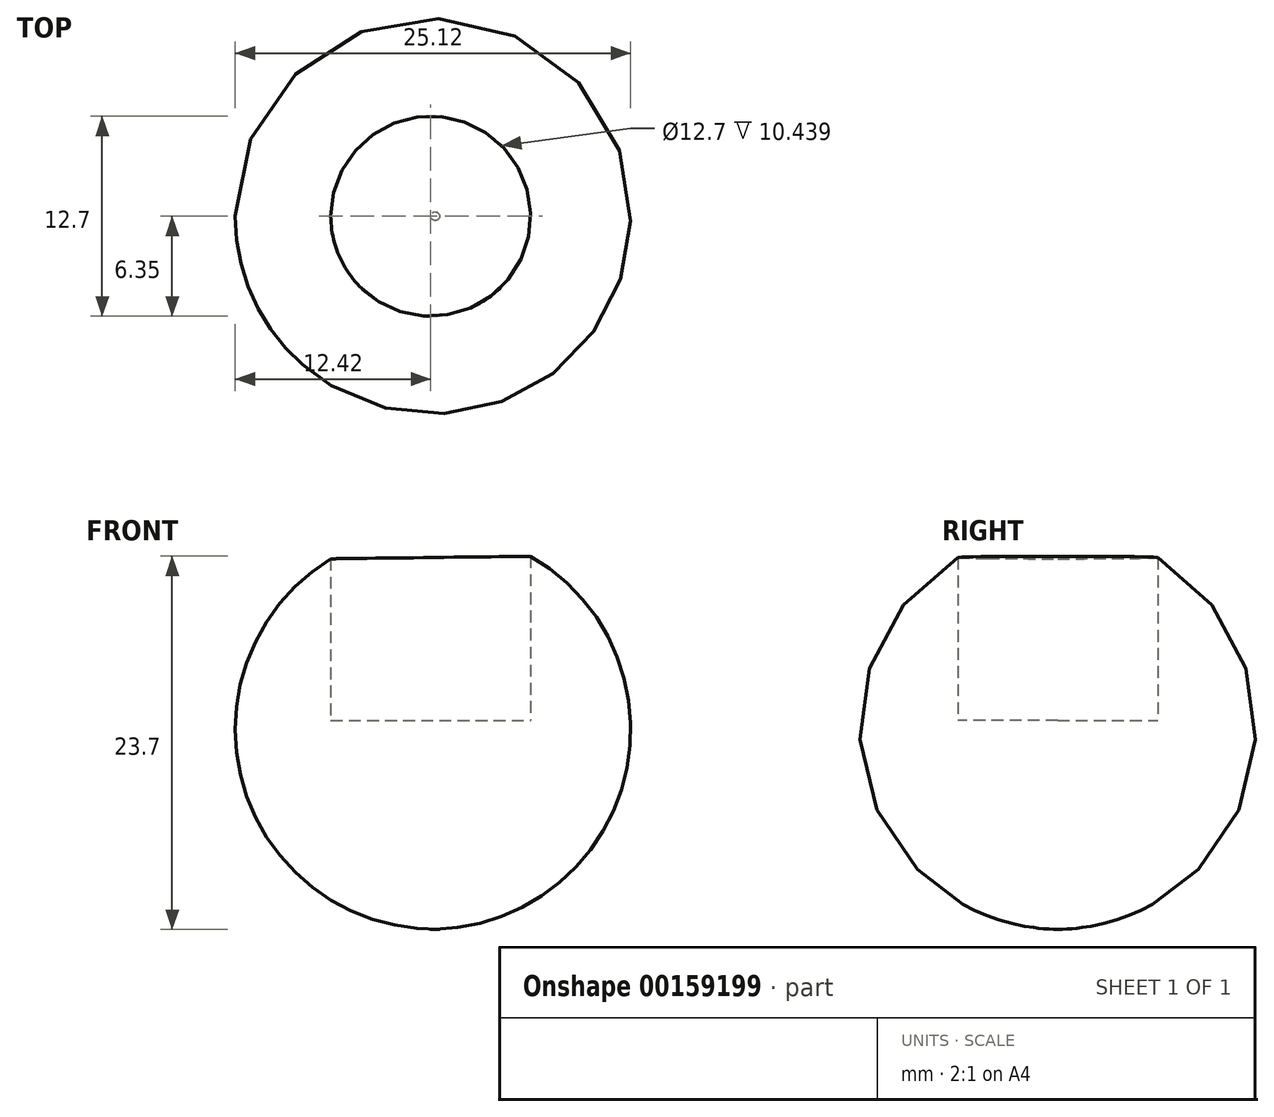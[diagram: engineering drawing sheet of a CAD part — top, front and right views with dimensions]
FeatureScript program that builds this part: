
annotation { "Feature Type Name" : "Feature", "Feature Type Description" : "" }
export const myFeature = defineFeature(function(context is Context, id is Id, definition is map)
    precondition{}
    {
        {
            var Q0;
            Q0=qCreatedBy(makeId("Front.planeOp"),FACE);
            var sketch = newSketch(context, id + "F0", { "sketchPlane" : qUnion([Q0])});
            skArc(sketch, "E0", {"start": v(0, 12.14) * mm, "mid": v(-12.42, -0.7) * mm, "end": v(0.28, -13.26) * mm});
            skLineSegment(sketch, "E1", {"start": v(0, 12.14) * mm, "end": v(0.28, -13.26) * mm});
            skSolve(sketch);
        }
        {
            var Q0;
            Q0=makeQuery(id+"F0.imprint","IMPRINT",FACE,{"disambiguationData":[TD([[makeQuery(id+"F0.imprint","IMPRINT",EDGE,{"derivedFrom":sQuery(id+"F0.wireOp",EDGE,"E0")}),1.0]])]});
            var Q1;
            Q1=sQuery(id+"F0.wireOp",EDGE,"E1");
            revolve(context, id + "F1", {"entities" : qUnion([Q0]), "axis" : qUnion([Q1]), "revolveType" : RevolveType.FULL});
        }
        {
            var Q0;
            Q0=qCreatedBy(makeId("Top.planeOp"),FACE);
            var sketch = newSketch(context, id + "F2", { "sketchPlane" : qUnion([Q0])});
            skCircle(sketch, "E2", {"center": v(0, 0) * mm, "radius": 6.35 * mm});
            skSolve(sketch);
        }
        {
            var Q0;
            Q0 = qSketchRegion(id + "F2", true);
            extrude(context, id + "F3", {"entities" : qUnion([Q0]), "operationType" : NewBodyOperationType.REMOVE, "depth" : 25.4 * mm});
        }
    });
